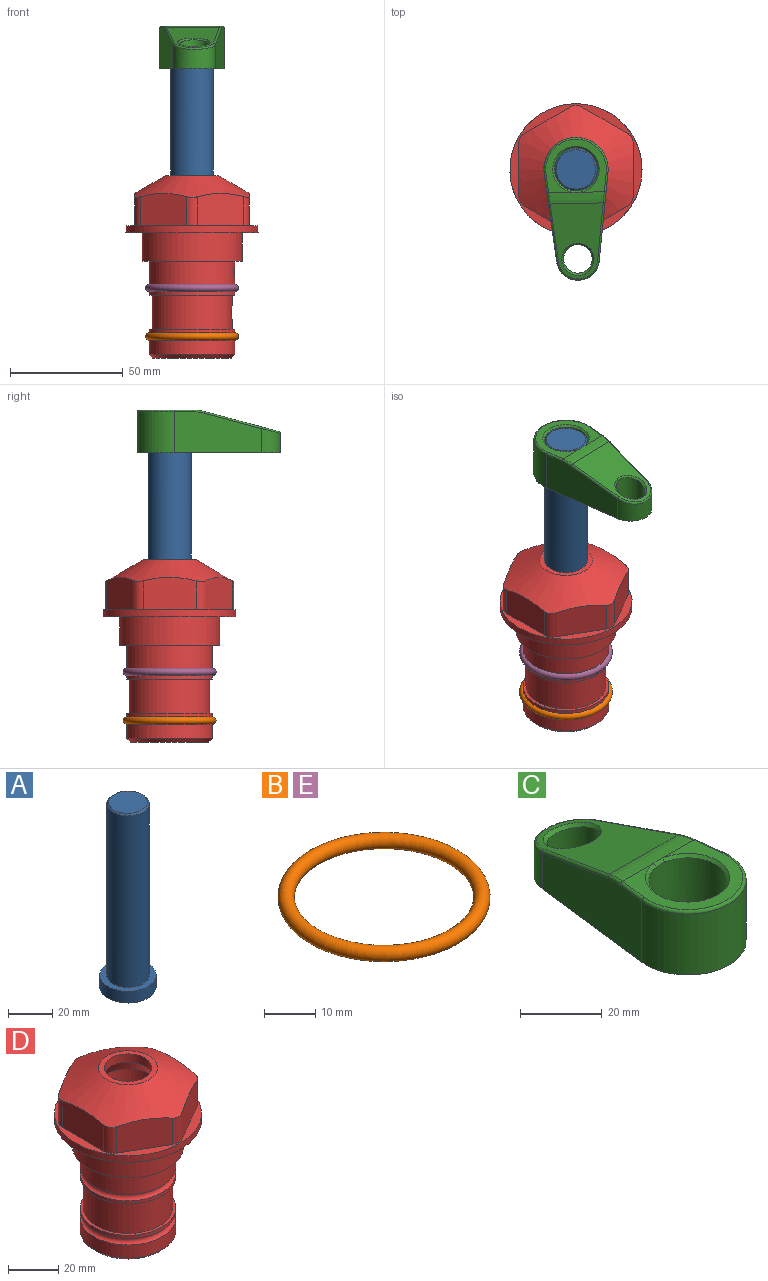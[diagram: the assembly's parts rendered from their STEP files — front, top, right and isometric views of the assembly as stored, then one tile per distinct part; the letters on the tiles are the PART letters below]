
ASSEMBLY  parts=5 mates=4
PART A: 6 faces, bbox 25.4x25.4x101.6 mm
  f0: plane 17.46x17.46mm, normal (0,0,1), area 239.5mm2, adj f5
  f1: plane 25.4x25.4mm, normal (0,0,-1), area 506.7mm2, adj f2
  f2: cylinder r=12.7mm len=25.4mm, axis (0,0,1), area 506.7mm2, adj f1,f3
  f3: plane 25.4x25.4mm, normal (0,0,1), area 221.7mm2, adj f2,f4
  f4: cylinder r=9.53mm len=94.46mm, axis (0,0,1), area 5653mm2, adj f3,f5
  f5: cone r=8.73mm half-angle=45deg, axis (0,0,-1), area 64.4mm2, adj f0,f4
PART B: 1 faces, bbox 44.7x44.7x3.2 mm
  f0: torus R=19.05mm, axis (0,0,1), area 1193.9mm2
PART C: 31 faces, bbox 31.7x65.5x19.8 mm
  f0: plane 39.12x18.26mm, normal (0.99,0.12,0), area 612.2mm2, adj f1,f4,f7,f11,f13,f15
  f1: cylinder r=9.53mm len=18.91mm, axis (0,0,-1), area 296.1mm2, adj f0,f2,f7,f17
  f2: plane 39.12x18.26mm, normal (-0.99,0.12,0), area 612.2mm2, adj f1,f4,f7,f12,f14,f16
  f3: cylinder r=6.35mm len=12.7mm, axis (0,0,-1), area 362.4mm2, adj f7,f18
  f4: cylinder r=14.29mm len=28.58mm, axis (0,0,-1), area 882.2mm2, adj f0,f2,f7,f10
  f5: cylinder r=9.53mm len=19.05mm, axis (0,0,-1), area 1092.6mm2, adj f7,f19,f20
  f6: plane 26.99x23.69mm, normal (0,0,1), area 216.2mm2, adj f9,f10,f11,f12,f19
  f7: plane 63.5x28.58mm, normal (0,0,-1), area 661.8mm2, adj f0,f1,f2,f3,f4,f5,f22,f23
  f8: plane 33.52x23.6mm, normal (0,0.26,0.97), area 486mm2, adj f9,f15,f16,f17,f18
  f9: cylinder r=19.05mm len=24.72mm, axis (1,0,0), area 120.4mm2, adj f6,f8,f13,f14,f20
  f10: torus R=13.49mm, axis (0,0,1), area 59mm2, adj f4,f6,f11,f12
  f11: cylinder r=0.79mm len=8.67mm, axis (0.12,-0.99,0), area 10.8mm2, adj f0,f6,f10,f13
  f12: cylinder r=0.79mm len=8.67mm, axis (0.12,0.99,0), area 10.8mm2, adj f2,f6,f10,f14
  f13: bspline ~4.95x1.42mm, area 6.1mm2, adj f0,f9,f11,f15
  f14: bspline ~4.95x1.42mm, area 6.1mm2, adj f2,f9,f12,f16
  f15: cylinder r=0.79mm len=25.95mm, axis (0.12,-0.96,0.26), area 32.9mm2, adj f0,f8,f13,f17
  f16: cylinder r=0.79mm len=25.95mm, axis (0.12,0.96,-0.26), area 32.9mm2, adj f2,f8,f14,f17
  f17: bspline ~18.91x8.38mm, area 30mm2, adj f1,f8,f15,f16
  f18: bspline ~14.29x14.29mm, area 48.3mm2, adj f3,f8
  f19: cone r=9.53mm half-angle=45deg, axis (0,0,1), area 66.5mm2, adj f5,f6,f20
  f20: bspline ~3.22x0.96mm, area 3.5mm2, adj f5,f9,f19
  f21: plane 2.75x2.72mm, normal (0,0,-1), area 2.9mm2, adj f23,f25,f28
  f22: plane 23.05x15.88mm, normal (-0.99,-0.12,0), area 323.6mm2, adj f7,f25,f26,f27,f28,f29
  f23: plane 23.05x15.88mm, normal (0.99,-0.12,0), area 323.6mm2, adj f7,f21,f25,f27,f28,f30
  f24: cylinder r=9.53mm len=10.69mm, axis (0,0,-1), area 114.7mm2, adj f7,f27,f29,f30
  f25: cylinder r=12.7mm len=20.59mm, axis (0,0,-1), area 381.1mm2, adj f7,f21,f22,f23,f26,f28
  f26: plane 2.75x2.72mm, normal (0,0,-1), area 2.9mm2, adj f22,f25,f28
  f27: plane 19.72x18.37mm, normal (0,-0.26,-0.97), area 291.8mm2, adj f22,f23,f24,f28,f29,f30
  f28: cylinder r=15.88mm len=19.92mm, axis (1,0,0), area 54.8mm2, adj f21,f22,f23,f25,f26,f27
  f29: cylinder r=1.59mm len=11mm, axis (0,0,-1), area 34.7mm2, adj f7,f22,f24,f27
  f30: cylinder r=1.59mm len=11mm, axis (0,0,-1), area 34.7mm2, adj f7,f23,f24,f27
PART D: 36 faces, bbox 58.7x58.7x81 mm
  f0: cylinder r=17.78mm len=35.56mm, axis (0,0,1), area 1670.8mm2, adj f23,f24,f31
  f1: cylinder r=19.05mm len=38.1mm, axis (0,0,1), area 1191.9mm2, adj f26,f27,f30
  f2: plane 58.66x58.66mm, normal (0,0,-1), area 1150.6mm2, adj f3,f28
  f3: cylinder r=29.33mm len=58.66mm, axis (0,0,-1), area 585.1mm2, adj f2,f4
  f4: plane 58.66x58.66mm, normal (0,0,1), area 475.9mm2, adj f3,f5,f6,f7,f8,f9,f10,f11
  f5: plane 20.32x14.34mm, normal (-0.5,0.87,0), area 324.4mm2, adj f4,f15,f16,f17
  f6: plane 20.32x14.34mm, normal (0.5,0.87,0), area 324.4mm2, adj f4,f14,f15,f17
  f7: plane 23.48x14.34mm, normal (1,0,0), area 324.4mm2, adj f4,f13,f14,f17
  f8: plane 20.32x14.34mm, normal (0.5,-0.87,0), area 324.4mm2, adj f4,f12,f13,f17
  f9: plane 20.32x14.34mm, normal (-0.5,-0.87,0), area 324.4mm2, adj f4,f11,f12,f17
  f10: plane 23.48x14.34mm, normal (-1,0,0), area 324.4mm2, adj f4,f11,f16,f17
  f11: cylinder r=5.08mm len=12.85mm, axis (0,0,-1), area 67.2mm2, adj f4,f9,f10,f17
  f12: cylinder r=5.08mm len=12.85mm, axis (0,0,-1), area 67.2mm2, adj f4,f8,f9,f17
  f13: cylinder r=5.08mm len=12.85mm, axis (0,0,-1), area 67.2mm2, adj f4,f7,f8,f17
  f14: cylinder r=5.08mm len=12.85mm, axis (0,0,-1), area 67.2mm2, adj f4,f6,f7,f17
  f15: cylinder r=5.08mm len=12.85mm, axis (0,0,-1), area 67.2mm2, adj f4,f5,f6,f17
  f16: cylinder r=5.08mm len=12.85mm, axis (0,0,-1), area 67.2mm2, adj f4,f5,f10,f17
  f17: cone r=11.73mm half-angle=60deg, axis (0,0,-1), area 2071.8mm2, adj f5,f6,f7,f8,f9,f10,f11,f12
  f18: plane 23.46x23.46mm, normal (0,0,1), area 147.4mm2, adj f17,f35
  f19: plane 34.93x34.93mm, normal (0,0,-1), area 958mm2, adj f29
  f20: cylinder r=19.05mm len=38.1mm, axis (0,0,1), area 760.1mm2, adj f21,f29
  f21: torus R=19.05mm, axis (0,0,1), area 565.3mm2, adj f20,f22
  f22: cylinder r=19.05mm len=38.1mm, axis (0,0,1), area 190mm2, adj f21,f23
  f23: plane 38.1x38.1mm, normal (0,0,1), area 146.9mm2, adj f0,f22
  f24: plane 38.1x38.1mm, normal (0,0,-1), area 146.9mm2, adj f0,f25
  f25: cylinder r=19.05mm len=38.1mm, axis (0,0,1), area 190mm2, adj f24,f26
  f26: torus R=19.05mm, axis (0,0,1), area 565.3mm2, adj f1,f25
  f27: plane 44.45x44.45mm, normal (0,0,-1), area 411.7mm2, adj f1,f28
  f28: cylinder r=22.23mm len=44.45mm, axis (0,0,1), area 1773.5mm2, adj f2,f27
  f29: cone r=19.05mm half-angle=45deg, axis (0,0,1), area 257.5mm2, adj f19,f20
  f30: cylinder r=3.17mm len=6.75mm, axis (-1,0,0), area 128mm2, adj f1,f33
  f31: cylinder r=3.17mm len=6.35mm, axis (-1,0,0), area 102.5mm2, adj f0,f33
  f32: plane 25.4x25.4mm, normal (0,0,1), area 506.7mm2, adj f33
  f33: cylinder r=12.7mm len=66.42mm, axis (0,0,-1), area 5236.2mm2, adj f30,f31,f32,f34
  f34: cone r=9.53mm half-angle=30deg, axis (0,0,-1), area 443.4mm2, adj f33,f35
  f35: cylinder r=9.53mm len=19.05mm, axis (0,0,-1), area 240.9mm2, adj f18,f34
PART E: same geometry as B
PLACE A rot(axis=(0,0,-1),178.7deg) t=(0,0,27.55)mm
PLACE B t=(0,0,-21.59)mm
PLACE C rot(axis=(0,0,-1),178.7deg) t=(0,0,28.35)mm
PLACE D at identity fixed
PLACE E at identity
MATE fastened D.f0 <-> B.f0  axis (0,0,1) through (0,0,-46.1)mm
MATE fastened A.f2 <-> C.f4  axis (0,0,1) through (0,0,91.05)mm
MATE fastened D.f0 <-> E.f0  axis (0,0,1) through (0,0,-24.51)mm
MATE cylindrical A.f2 <-> D.f0  axis (0,0,-1) through (0,0,-10.55)mm
